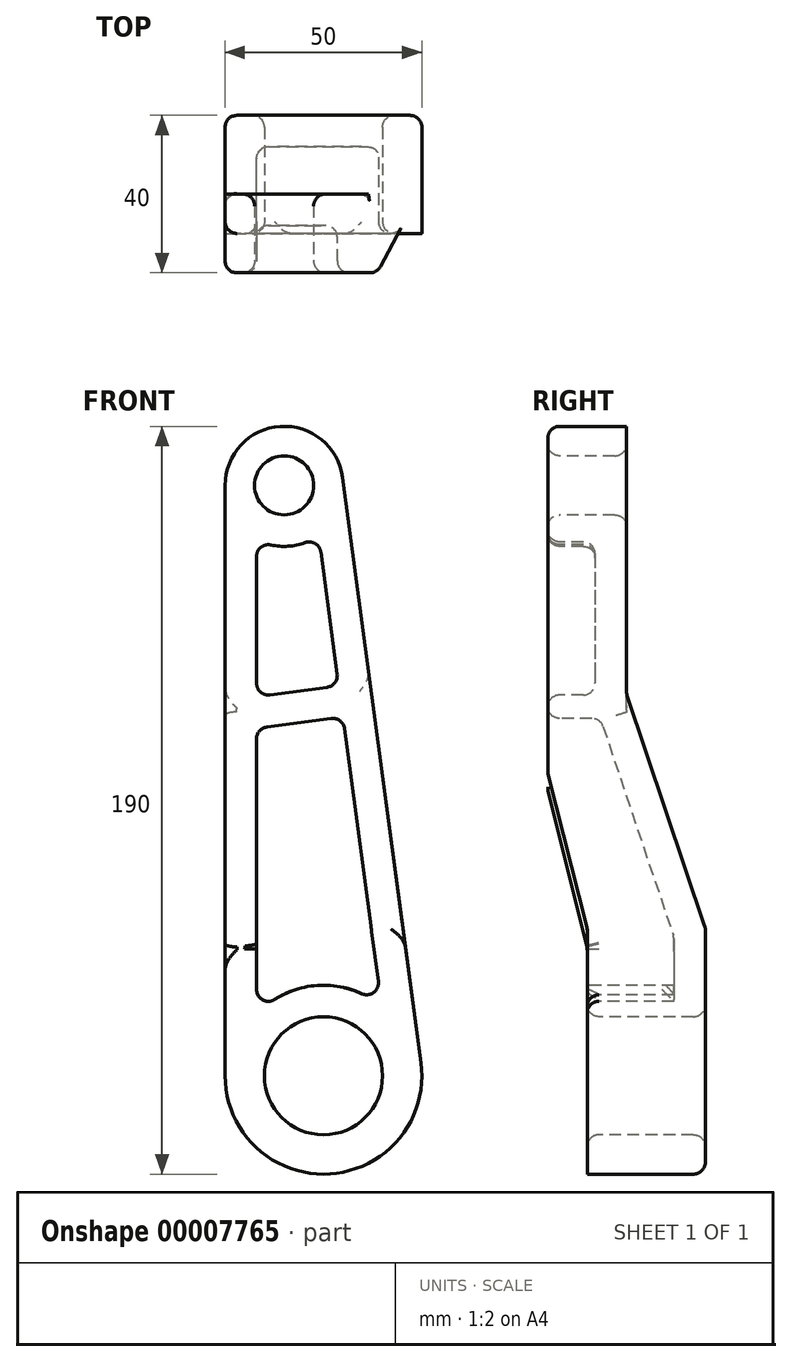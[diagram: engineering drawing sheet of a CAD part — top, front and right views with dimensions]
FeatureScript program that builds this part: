
annotation { "Feature Type Name" : "Feature", "Feature Type Description" : "" }
export const myFeature = defineFeature(function(context is Context, id is Id, definition is map)
    precondition{}
    {
        {
            var Q0;
            Q0=qCreatedBy(makeId("Front.planeOp"),FACE);
            var sketch = newSketch(context, id + "F0", { "sketchPlane" : qUnion([Q0])});
            skArc(sketch, "E0", {"start": v(-25, 0) * mm, "mid": v(1.66, -24.94) * mm, "end": v(24.78, 3.32) * mm});
            skArc(sketch, "E1", {"start": v(4.87, 152) * mm, "mid": v(-11, 164.97) * mm, "end": v(-25, 150) * mm});
            skLineSegment(sketch, "E2", {"start": v(-25, 150) * mm, "end": v(-25, 0) * mm});
            skLineSegment(sketch, "E3", {"start": v(4.87, 152) * mm, "end": v(24.78, 3.32) * mm});
            skSolve(sketch);
        }
        {
            var Q0;
            Q0 = qSketchRegion(id + "F0", true);
            extrude(context, id + "F1", {"entities" : qUnion([Q0]), "depth" : 40 * mm});
        }
        {
            var Q0;
            Q0=makeQuery(id+"F1.opExtrude","SWEPT_FACE",FACE,{"disambiguationData":[OSD([sQuery(id+"F0.wireOp",EDGE,"E3")])]});
            var sketch = newSketch(context, id + "F2", { "sketchPlane" : qUnion([Q0])});
            skLineSegment(sketch, "E4", {"start": v(-20, 165) * mm, "end": v(-20, 95) * mm});
            skLineSegment(sketch, "E5", {"start": v(-20, 95) * mm, "end": v(0, 35) * mm});
            skLineSegment(sketch, "E6", {"start": v(0, 35) * mm, "end": v(0, 165) * mm});
            skLineSegment(sketch, "E7", {"start": v(0, 165) * mm, "end": v(-20, 165) * mm});
            skLineSegment(sketch, "E8", {"start": v(-30, -25) * mm, "end": v(-30, 35) * mm});
            skLineSegment(sketch, "E9", {"start": v(-30, 35) * mm, "end": v(-40, 75) * mm});
            skLineSegment(sketch, "E10", {"start": v(-40, 75) * mm, "end": v(-40, -25) * mm});
            skLineSegment(sketch, "E11", {"start": v(-40, -25) * mm, "end": v(-30, -25) * mm});
            skLineSegment(sketch, "E12.0", {"start": v(-40, -25) * mm, "end": v(-40, 3.32) * mm, "construction": true});
            skLineSegment(sketch, "E13.0", {"start": v(0, 150) * mm, "end": v(0, 165) * mm, "construction": true});
            skSolve(sketch);
        }
        {
            var Q0;
            Q0 = qSketchRegion(id + "F2", true);
            extrude(context, id + "F3", {"entities" : qUnion([Q0]), "operationType" : NewBodyOperationType.REMOVE, "endBound" : BoundingType.THROUGH_ALL, "oppositeDirection" : true, "depth" : 25 * mm});
        }
        {
            var Q0;
            Q0=makeQuery(id+"F1.opExtrude","CAP_FACE",FACE,{"disambiguationData":[OSD([sQuery(id+"F0.wireOp",EDGE,"E0"),sQuery(id+"F0.wireOp",EDGE,"E1"),sQuery(id+"F0.wireOp",EDGE,"E2"),sQuery(id+"F0.wireOp",EDGE,"E3")])],"isStart":false});
            var sketch = newSketch(context, id + "F4", { "sketchPlane" : qUnion([Q0])});
            skCircle(sketch, "E14", {"center": v(-10, 150) * mm, "radius": 7.5 * mm});
            skCircle(sketch, "E15", {"center": v(0, 0) * mm, "radius": 15 * mm});
            skSolve(sketch);
        }
        {
            var Q0;
            Q0 = qSketchRegion(id + "F4", true);
            extrude(context, id + "F5", {"entities" : qUnion([Q0]), "operationType" : NewBodyOperationType.REMOVE, "endBound" : BoundingType.THROUGH_ALL, "oppositeDirection" : true, "depth" : 25 * mm});
        }
        {
            var Q0;
            Q0=makeQuery(id+"F1.opExtrude","CAP_FACE",FACE,{"disambiguationData":[OSD([sQuery(id+"F0.wireOp",EDGE,"E0"),sQuery(id+"F0.wireOp",EDGE,"E1"),sQuery(id+"F0.wireOp",EDGE,"E2"),sQuery(id+"F0.wireOp",EDGE,"E3")])],"isStart":false});
            var Q1;
            Q1=makeQuery(id+"F3.boolean.opBoolean","COPY",FACE,{"derivedFrom":makeQuery(id+"F3.opExtrude","SWEPT_FACE",FACE,{"disambiguationData":[OSD([sQuery(id+"F2.wireOp",EDGE,"E9")])]})});
            var Q2;
            Q2=makeQuery(id+"F3.boolean.opBoolean","COPY",FACE,{"derivedFrom":makeQuery(id+"F3.opExtrude","SWEPT_FACE",FACE,{"disambiguationData":[OSD([sQuery(id+"F2.wireOp",EDGE,"E8")])]})});
            shell(context, id + "F6", {"entities" : qUnion([Q0, Q1, Q2]), "thickness" : 8 * mm});
        }
        {
            var Q0;
            Q0=makeQuery(id+"F1.opExtrude","CAP_FACE",FACE,{"disambiguationData":[OSD([sQuery(id+"F0.wireOp",EDGE,"E0"),sQuery(id+"F0.wireOp",EDGE,"E1"),sQuery(id+"F0.wireOp",EDGE,"E2"),sQuery(id+"F0.wireOp",EDGE,"E3")])],"isStart":false});
            var sketch = newSketch(context, id + "F7", { "sketchPlane" : qUnion([Q0])});
            skLineSegment(sketch, "E16.0", {"start": v(-17, 92.26) * mm, "end": v(4.41, 95.13) * mm, "construction": true});
            skLineSegment(sketch, "E17.1", {"start": v(-17, 96.3) * mm, "end": v(-17, 88.23) * mm});
            skLineSegment(sketch, "E17.2", {"start": v(3.88, 99.1) * mm, "end": v(4.94, 91.16) * mm});
            skLineSegment(sketch, "E18", {"start": v(-17, 96.3) * mm, "end": v(3.88, 99.1) * mm});
            skLineSegment(sketch, "E19.0.MirrorCS", {"start": v(-17, 88.23) * mm, "end": v(4.94, 91.16) * mm});
            skSolve(sketch);
        }
        {
            var Q0;
            Q0 = qSketchRegion(id + "F7", true);
            var Q1;
            Q1=makeQuery(id+"F6.opShell","OFFSET_FACE",FACE,{"disambiguationData":[OSD([sQuery(id+"F2.wireOp",EDGE,"E4")])]});
            extrude(context, id + "F8", {"entities" : qUnion([Q0]), "operationType" : NewBodyOperationType.ADD, "endBound" : BoundingType.UP_TO_BODY, "oppositeDirection" : true, "endBoundEntityBody" : qUnion([Q1]), "depth" : 25 * mm});
        }
        {
            var Q0;
            Q0=makeQuery(id+"F6.opShell","OFFSET_FACE",FACE,{"disambiguationData":[OSD([sQuery(id+"F2.wireOp",EDGE,"E4")])]});
            var Q1;
            {var subQ0=sQuery(id+"F0.wireOp",EDGE,"E3");Q1=makeQuery(id+"F8.boolean.opBoolean","SPLIT",FACE,{"disambiguationData":[TD([makeQuery(id+"F6.opShell","OFFSET_FACE",FACE,{"disambiguationData":[OSD([sQuery(id+"F4.wireOp",EDGE,"E14")])]})])],"derivedFrom":makeQuery(id+"F6.opShell","OFFSET_FACE",FACE,{"disambiguationData":[OSD([subQ0])]})});}
            var Q2;
            {var subQ0=sQuery(id+"F0.wireOp",EDGE,"E2");Q2=makeQuery(id+"F8.boolean.opBoolean","SPLIT",FACE,{"disambiguationData":[TD([makeQuery(id+"F6.opShell","OFFSET_FACE",FACE,{"disambiguationData":[OSD([sQuery(id+"F4.wireOp",EDGE,"E14")])]})])],"derivedFrom":makeQuery(id+"F6.opShell","OFFSET_FACE",FACE,{"disambiguationData":[OSD([subQ0])]})});}
            var Q3;
            Q3=makeQuery(id+"F6.opShell","OFFSET_FACE",FACE,{"disambiguationData":[OSD([sQuery(id+"F2.wireOp",EDGE,"E5")])]});
            var Q4;
            Q4=makeQuery(id+"F8.opExtrude","SWEPT_FACE",FACE,{"disambiguationData":[OSD([sQuery(id+"F7.wireOp",EDGE,"E19.0.MirrorCS")])]});
            var Q5;
            {var subQ0=sQuery(id+"F0.wireOp",EDGE,"E3");Q5=makeQuery(id+"F8.boolean.opBoolean","SPLIT",FACE,{"disambiguationData":[TD([makeQuery(id+"F3.boolean.opBoolean","COPY",FACE,{"derivedFrom":makeQuery(id+"F3.opExtrude","SWEPT_FACE",FACE,{"disambiguationData":[OSD([sQuery(id+"F2.wireOp",EDGE,"E8")])]})})])],"derivedFrom":makeQuery(id+"F6.opShell","OFFSET_FACE",FACE,{"disambiguationData":[OSD([subQ0])]})});}
            var Q6;
            {var subQ0=sQuery(id+"F0.wireOp",EDGE,"E2");Q6=makeQuery(id+"F8.boolean.opBoolean","SPLIT",FACE,{"disambiguationData":[TD([makeQuery(id+"F3.boolean.opBoolean","COPY",FACE,{"derivedFrom":makeQuery(id+"F3.opExtrude","SWEPT_FACE",FACE,{"disambiguationData":[OSD([sQuery(id+"F2.wireOp",EDGE,"E8")])]})})])],"derivedFrom":makeQuery(id+"F6.opShell","OFFSET_FACE",FACE,{"disambiguationData":[OSD([subQ0])]})});}
            var Q7;
            Q7=makeQuery(id+"F8.boolean.opBoolean","MERGE",FACE,{"derivedFrom":[makeQuery(id+"F1.opExtrude","CAP_FACE",FACE,{"disambiguationData":[OSD([sQuery(id+"F0.wireOp",EDGE,"E0"),sQuery(id+"F0.wireOp",EDGE,"E1"),sQuery(id+"F0.wireOp",EDGE,"E2"),sQuery(id+"F0.wireOp",EDGE,"E3")])],"isStart":false}),makeQuery(id+"F8.opExtrude","CAP_FACE",FACE,{"disambiguationData":[OSD([sQuery(id+"F7.wireOp",EDGE,"E17.1"),sQuery(id+"F7.wireOp",EDGE,"E17.2"),sQuery(id+"F7.wireOp",EDGE,"E18"),sQuery(id+"F7.wireOp",EDGE,"E19.0.MirrorCS")])],"isStart":true})]});
            var Q8;
            Q8=makeQuery(id+"F3.boolean.opBoolean","COPY",FACE,{"derivedFrom":makeQuery(id+"F3.opExtrude","SWEPT_FACE",FACE,{"disambiguationData":[OSD([sQuery(id+"F2.wireOp",EDGE,"E9")])]})});
            var Q9;
            Q9=makeQuery(id+"F6.opShell","OFFSET_FACE",FACE,{"disambiguationData":[OSD([sQuery(id+"F2.wireOp",EDGE,"E9")])]});
            var Q10;
            Q10=makeQuery(id+"F5.boolean.opBoolean","COPY",FACE,{"derivedFrom":makeQuery(id+"F5.opExtrude","SWEPT_FACE",FACE,{"disambiguationData":[OSD([sQuery(id+"F4.wireOp",EDGE,"E15")])]})});
            var Q11;
            Q11=makeQuery(id+"F1.opExtrude","CAP_FACE",FACE,{"disambiguationData":[OSD([sQuery(id+"F0.wireOp",EDGE,"E0"),sQuery(id+"F0.wireOp",EDGE,"E1"),sQuery(id+"F0.wireOp",EDGE,"E2"),sQuery(id+"F0.wireOp",EDGE,"E3")])],"isStart":true});
            var Q12;
            Q12=makeQuery(id+"F3.boolean.opBoolean","COPY",FACE,{"derivedFrom":makeQuery(id+"F3.opExtrude","SWEPT_FACE",FACE,{"disambiguationData":[OSD([sQuery(id+"F2.wireOp",EDGE,"E5")])]})});
            var Q13;
            Q13=makeQuery(id+"F5.boolean.opBoolean","COPY",FACE,{"derivedFrom":makeQuery(id+"F5.opExtrude","SWEPT_FACE",FACE,{"disambiguationData":[OSD([sQuery(id+"F4.wireOp",EDGE,"E14")])]})});
            fillet(context, id + "F9", {"entities" : qUnion([Q0, Q1, Q2, Q3, Q4, Q5, Q6, Q7, Q8, Q9, Q10, Q11, Q12, Q13]), "radius" : 3 * mm, "tangentPropagation" : true, "allowEdgeOverflow" : false});
        }
    });
